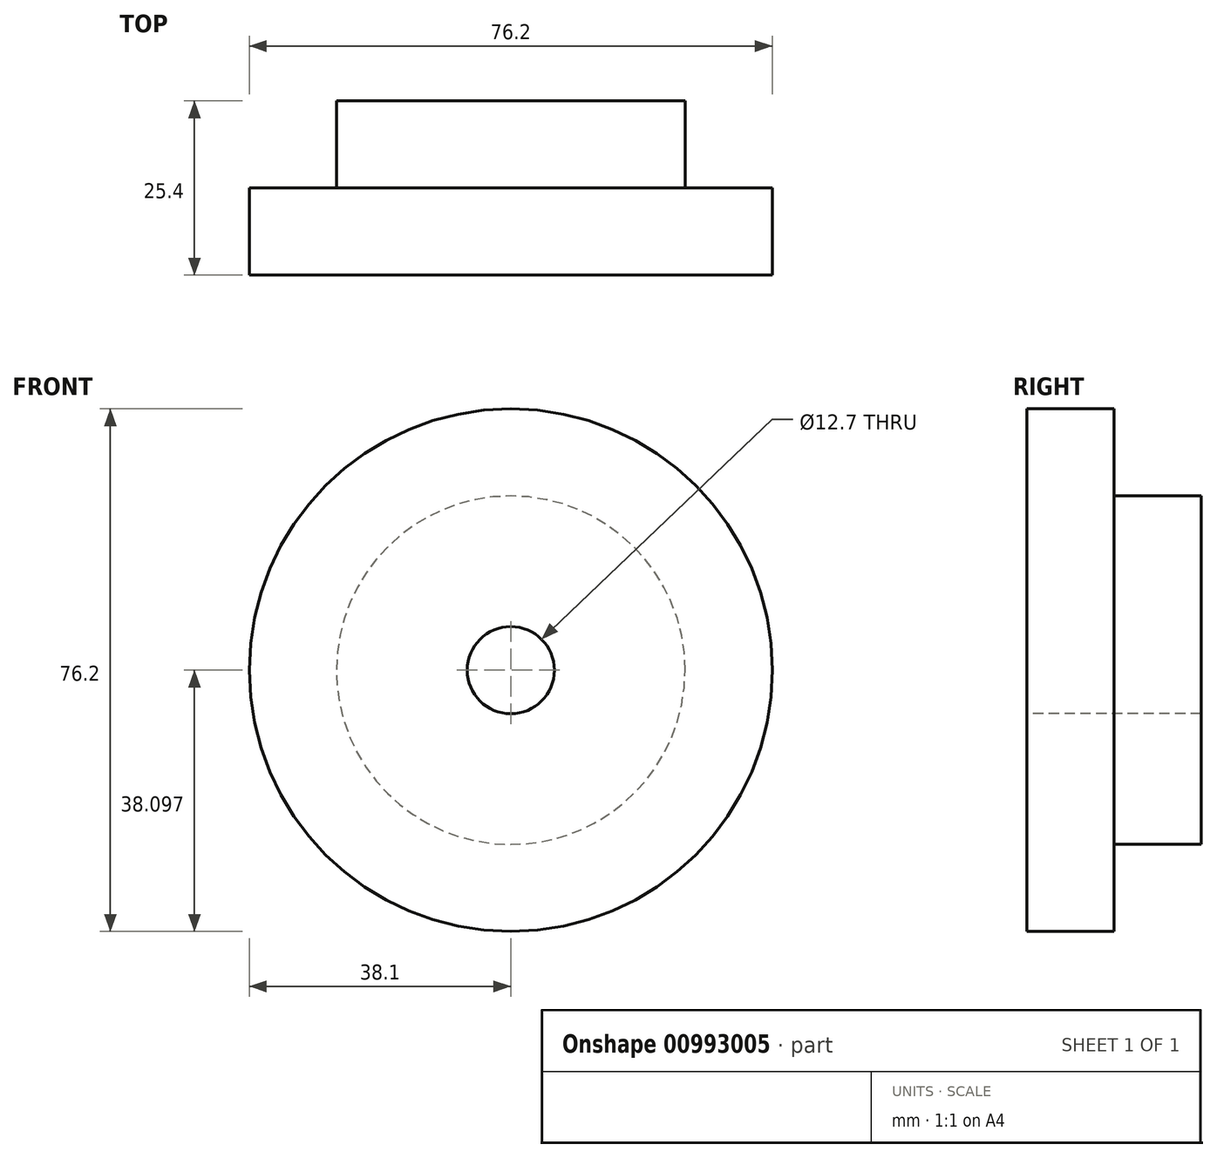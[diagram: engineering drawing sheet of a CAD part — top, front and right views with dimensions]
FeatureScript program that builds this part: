
annotation { "Feature Type Name" : "Feature", "Feature Type Description" : "" }
export const myFeature = defineFeature(function(context is Context, id is Id, definition is map)
    precondition{}
    {
        {
            var Q0;
            Q0=qCreatedBy(makeId("Right.planeOp"),FACE);
            var sketch = newSketch(context, id + "F0", { "sketchPlane" : qUnion([Q0])});
            skLineSegment(sketch, "E0", {"start": v(-63.44, -23.07) * mm, "end": v(-29.07, -23.07) * mm, "construction": true});
            skLineSegment(sketch, "E1.bottom", {"start": v(-63.44, -16.72) * mm, "end": v(-50.74, -16.72) * mm});
            skLineSegment(sketch, "E1.top", {"start": v(-63.44, 15.03) * mm, "end": v(-50.74, 15.03) * mm});
            skLineSegment(sketch, "E1.left", {"start": v(-63.44, -16.72) * mm, "end": v(-63.44, 15.03) * mm});
            skLineSegment(sketch, "E1.right", {"start": v(-50.74, -16.72) * mm, "end": v(-50.74, 15.03) * mm});
            skLineSegment(sketch, "E2.bottom", {"start": v(-63.44, -16.72) * mm, "end": v(-38.04, -16.72) * mm});
            skLineSegment(sketch, "E2.top", {"start": v(-63.44, 2.33) * mm, "end": v(-38.04, 2.33) * mm});
            skLineSegment(sketch, "E2.left", {"start": v(-63.44, -16.72) * mm, "end": v(-63.44, 2.33) * mm});
            skLineSegment(sketch, "E2.right", {"start": v(-38.04, -16.72) * mm, "end": v(-38.04, 2.33) * mm});
            skLineSegment(sketch, "E3.MirrorCS", {"start": v(-63.44, -61.17) * mm, "end": v(-50.74, -61.17) * mm});
            skLineSegment(sketch, "E4.MirrorCS", {"start": v(-63.44, -29.42) * mm, "end": v(-50.74, -29.42) * mm});
            skLineSegment(sketch, "E5.MirrorCS", {"start": v(-63.44, -29.42) * mm, "end": v(-63.44, -48.47) * mm});
            skLineSegment(sketch, "E6.MirrorCS", {"start": v(-63.44, -48.47) * mm, "end": v(-38.04, -48.47) * mm});
            skLineSegment(sketch, "E7.MirrorCS", {"start": v(-38.04, -29.42) * mm, "end": v(-38.04, -48.47) * mm});
            skLineSegment(sketch, "E8.MirrorCS", {"start": v(-63.44, -29.42) * mm, "end": v(-63.44, -61.17) * mm});
            skLineSegment(sketch, "E9.MirrorCS", {"start": v(-50.74, -29.42) * mm, "end": v(-50.74, -61.17) * mm});
            skLineSegment(sketch, "E10.MirrorCS", {"start": v(-63.44, -29.42) * mm, "end": v(-38.04, -29.42) * mm});
            skSolve(sketch);
        }
        {
            var Q0;
            {var subQ0=sQuery(id+"F0.wireOp",EDGE,"E1.top");Q0=makeQuery(id+"F0.imprint","IMPRINT",FACE,{"disambiguationData":[TD([[makeQuery(id+"F0.imprint","IMPRINT",EDGE,{"derivedFrom":subQ0}),-1.0]])]});}
            var Q1;
            {var subQ0=sQuery(id+"F0.wireOp",EDGE,"E1.bottom");Q1=makeQuery(id+"F0.imprint","IMPRINT",FACE,{"disambiguationData":[TD([[makeQuery(id+"F0.imprint","IMPRINT",EDGE,{"derivedFrom":subQ0}),1.0]])]});}
            var Q2;
            {var subQ0=sQuery(id+"F0.wireOp",EDGE,"E2.bottom");Q2=makeQuery(id+"F0.imprint","IMPRINT",FACE,{"disambiguationData":[TD([[makeQuery(id+"F0.imprint","IMPRINT",EDGE,{"derivedFrom":subQ0}),1.0]])]});}
            var Q3;
            Q3=sQuery(id+"F0.wireOp",EDGE,"E0");
            revolve(context, id + "F1", {"surfaceOperationType" : NewSurfaceOperationType.NEW, "entities" : qUnion([Q0, Q1, Q2]), "axis" : qUnion([Q3]), "revolveType" : RevolveType.FULL});
        }
    });
